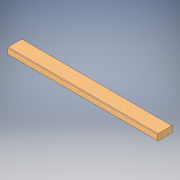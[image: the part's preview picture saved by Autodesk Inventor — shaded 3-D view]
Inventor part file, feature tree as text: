
AUTODESK INVENTOR PART (.ipt)
format: ipt  version: 2019 (Build 230136000, 136)  size: 112,128 bytes
history: native  units: in
note: dims shown in document units (in); Inventor stores cm internally (conversion verified against a paired STEP export)
features: extrude x1, fillet x1, sketch x1
ambient origin geometry x8: Origin, YZ Plane, XZ Plane, XY Plane, X Axis, Y Axis, Z Axis, Center Point
bodies: Solid1 (feature_tree)
feature tree (3):
  extrude  "Extrusion1"  Depth=3.5in
  fillet  "Fillet1"  Radius=35.4331in
  sketch  "Sketch1"  dims[d0=1.5in d1=3.5in d2=35.4331in d3=0.0in d4=0.125in]
